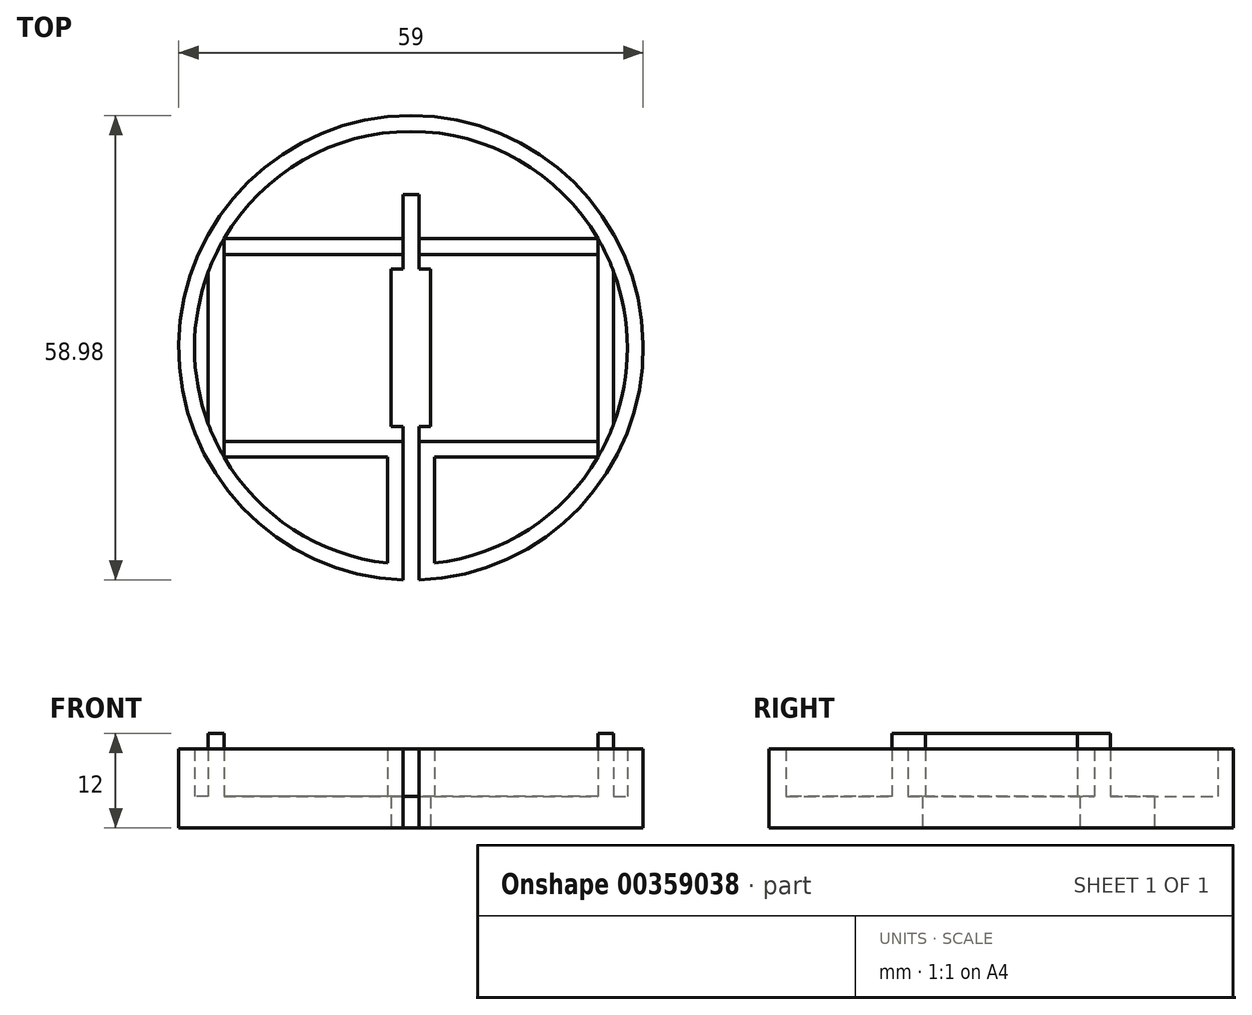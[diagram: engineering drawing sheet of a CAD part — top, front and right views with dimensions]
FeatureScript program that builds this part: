
annotation { "Feature Type Name" : "Feature", "Feature Type Description" : "" }
export const myFeature = defineFeature(function(context is Context, id is Id, definition is map)
    precondition{}
    {
        {
            var Q0;
            Q0=qCreatedBy(makeId("Top.planeOp"),FACE);
            var sketch = newSketch(context, id + "F0", { "sketchPlane" : qUnion([Q0])});
            skCircle(sketch, "E0", {"center": v(0, 0) * mm, "radius": 29.5 * mm});
            skPoint(sketch, "E1.middle", {"position": v(0, 29.5) * mm});
            skLineSegment(sketch, "E2.top", {"start": v(-1, -29.48) * mm, "end": v(1, -29.48) * mm});
            skLineSegment(sketch, "E2.left", {"start": v(-1, 29.48) * mm, "end": v(-1, -29.48) * mm});
            skLineSegment(sketch, "E2.right", {"start": v(1, 29.48) * mm, "end": v(1, -29.48) * mm});
            skLineSegment(sketch, "E3.bottom", {"start": v(-2.5, 10) * mm, "end": v(2.5, 10) * mm});
            skLineSegment(sketch, "E3.top", {"start": v(-2.5, -10) * mm, "end": v(2.5, -10) * mm});
            skLineSegment(sketch, "E3.left", {"start": v(-2.5, 10) * mm, "end": v(-2.5, -10) * mm});
            skLineSegment(sketch, "E3.right", {"start": v(2.5, 10) * mm, "end": v(2.5, -10) * mm});
            skLineSegment(sketch, "E4.top", {"start": v(-1, 19.48) * mm, "end": v(1, 19.48) * mm});
            skLineSegment(sketch, "E4.left", {"start": v(-1, 29.48) * mm, "end": v(-1, 19.48) * mm});
            skLineSegment(sketch, "E4.right", {"start": v(1, 29.48) * mm, "end": v(1, 19.48) * mm});
            skLineSegment(sketch, "E5", {"start": v(-23.75, 17.5) * mm, "end": v(-23.75, -17.5) * mm});
            skLineSegment(sketch, "E6", {"start": v(23.75, 17.5) * mm, "end": v(23.75, -17.5) * mm});
            skLineSegment(sketch, "E7", {"start": v(25.75, 14.4) * mm, "end": v(25.75, -14.4) * mm});
            skCircle(sketch, "E8", {"center": v(0, 0) * mm, "radius": 27.5 * mm});
            skLineSegment(sketch, "E9", {"start": v(-25.75, 14.4) * mm, "end": v(-25.75, -14.4) * mm});
            skLineSegment(sketch, "E10", {"start": v(-23.75, 13.87) * mm, "end": v(23.75, 13.87) * mm});
            skLineSegment(sketch, "E11", {"start": v(-23.75, 11.87) * mm, "end": v(23.75, 11.87) * mm});
            skLineSegment(sketch, "E12", {"start": v(-23.75, -13.87) * mm, "end": v(23.75, -13.87) * mm});
            skLineSegment(sketch, "E13", {"start": v(-23.75, -11.87) * mm, "end": v(23.75, -11.87) * mm});
            skLineSegment(sketch, "E14", {"start": v(-3, -27.34) * mm, "end": v(-3, -13.87) * mm});
            skLineSegment(sketch, "E15", {"start": v(3, -13.87) * mm, "end": v(3, -27.34) * mm});
            skSolve(sketch);
        }
        {
            var Q0;
            {var subQ0=sQuery(id+"F0.wireOp",EDGE,"E3.left");Q0=makeQuery(id+"F0.imprint","IMPRINT",FACE,{"disambiguationData":[TD([[makeQuery(id+"F0.imprint","IMPRINT",EDGE,{"derivedFrom":subQ0}),-1.0]])]});}
            var Q1;
            {var subQ1=sQuery(id+"F0.wireOp",EDGE,"E5");var subQ8=makeQuery(id+"F0.imprint","INTERSECT",VERTEX,{"derivedFrom":[subQ1,sQuery(id+"F0.wireOp",EDGE,"E11")]});Q1=makeQuery(id+"F0.imprint","IMPRINT",FACE,{"disambiguationData":[TD([[makeQuery(id+"F0.imprint","IMPRINT",EDGE,{"disambiguationData":[TD([[subQ8,-1.0]])],"derivedFrom":subQ1}),-1.0]])]});}
            var Q2;
            {var subQ0=sQuery(id+"F0.wireOp",EDGE,"E9");var subQ1=sQuery(id+"F0.wireOp",EDGE,"E8");var subQ2=makeQuery(id+"F0.imprint","INTERSECT",VERTEX,{"disambiguationData":[OD(0.0)],"derivedFrom":[subQ1,subQ0]});Q2=makeQuery(id+"F0.imprint","IMPRINT",FACE,{"disambiguationData":[TD([[makeQuery(id+"F0.imprint","IMPRINT",EDGE,{"disambiguationData":[TD([[subQ2,-1.0]])],"derivedFrom":subQ1}),1.0]])]});}
            var Q3;
            {var subQ0=sQuery(id+"F0.wireOp",EDGE,"E9");var subQ1=sQuery(id+"F0.wireOp",EDGE,"E0");var subQ2=makeQuery(id+"F0.imprint","INTERSECT",VERTEX,{"disambiguationData":[OD(0.0)],"derivedFrom":[subQ1,subQ0]});Q3=makeQuery(id+"F0.imprint","IMPRINT",FACE,{"disambiguationData":[TD([[makeQuery(id+"F0.imprint","IMPRINT",EDGE,{"disambiguationData":[TD([[subQ2,-1.0]])],"derivedFrom":subQ1}),1.0]])]});}
            var Q4;
            {var subQ0=sQuery(id+"F0.wireOp",EDGE,"E5");var subQ1=sQuery(id+"F0.wireOp",EDGE,"E0");var subQ2=makeQuery(id+"F0.imprint","INTERSECT",VERTEX,{"disambiguationData":[OD(0.0)],"derivedFrom":[subQ1,subQ0]});Q4=makeQuery(id+"F0.imprint","IMPRINT",FACE,{"disambiguationData":[TD([[makeQuery(id+"F0.imprint","IMPRINT",EDGE,{"disambiguationData":[TD([[subQ2,-1.0]])],"derivedFrom":subQ1}),1.0]])]});}
            var Q5;
            {var subQ0=sQuery(id+"F0.wireOp",EDGE,"E4.left");var subQ1=sQuery(id+"F0.wireOp",EDGE,"E0");var subQ2=makeQuery(id+"F0.imprint","INTERSECT",VERTEX,{"derivedFrom":[subQ1,subQ0]});Q5=makeQuery(id+"F0.imprint","IMPRINT",FACE,{"disambiguationData":[TD([[makeQuery(id+"F0.imprint","IMPRINT",EDGE,{"disambiguationData":[TD([[subQ2,-1.0]])],"derivedFrom":subQ1}),1.0]])]});}
            var Q6;
            {var subQ1=sQuery(id+"F0.wireOp",EDGE,"E2.left");var subQ3=sQuery(id+"F0.wireOp",EDGE,"E10");var subQ4=makeQuery(id+"F0.imprint","INTERSECT",VERTEX,{"derivedFrom":[subQ1,subQ3]});Q6=makeQuery(id+"F0.imprint","IMPRINT",FACE,{"disambiguationData":[TD([[makeQuery(id+"F0.imprint","IMPRINT",EDGE,{"disambiguationData":[TD([[subQ4,1.0]])],"derivedFrom":subQ1}),-1.0]])]});}
            var Q7;
            {var subQ0=sQuery(id+"F0.wireOp",EDGE,"E10");var subQ1=sQuery(id+"F0.wireOp",EDGE,"E2.left");var subQ2=makeQuery(id+"F0.imprint","INTERSECT",VERTEX,{"derivedFrom":[subQ1,subQ0]});Q7=makeQuery(id+"F0.imprint","IMPRINT",FACE,{"disambiguationData":[TD([[makeQuery(id+"F0.imprint","IMPRINT",EDGE,{"disambiguationData":[TD([[subQ2,-1.0]])],"derivedFrom":subQ1}),-1.0]])]});}
            var Q8;
            {var subQ0=sQuery(id+"F0.wireOp",EDGE,"E4.right");var subQ1=sQuery(id+"F0.wireOp",EDGE,"E0");var subQ2=makeQuery(id+"F0.imprint","INTERSECT",VERTEX,{"derivedFrom":[subQ1,subQ0]});Q8=makeQuery(id+"F0.imprint","IMPRINT",FACE,{"disambiguationData":[TD([[makeQuery(id+"F0.imprint","IMPRINT",EDGE,{"disambiguationData":[TD([[subQ2,1.0]])],"derivedFrom":subQ1}),1.0]])]});}
            var Q9;
            {var subQ0=sQuery(id+"F0.wireOp",EDGE,"E4.left");var subQ1=sQuery(id+"F0.wireOp",EDGE,"E0");var subQ2=makeQuery(id+"F0.imprint","INTERSECT",VERTEX,{"derivedFrom":[subQ1,subQ0]});Q9=makeQuery(id+"F0.imprint","IMPRINT",FACE,{"disambiguationData":[TD([[makeQuery(id+"F0.imprint","IMPRINT",EDGE,{"disambiguationData":[TD([[subQ2,1.0]])],"derivedFrom":subQ1}),1.0]])]});}
            var Q10;
            {var subQ0=sQuery(id+"F0.wireOp",EDGE,"E4.top");Q10=makeQuery(id+"F0.imprint","IMPRINT",FACE,{"disambiguationData":[TD([[makeQuery(id+"F0.imprint","IMPRINT",EDGE,{"derivedFrom":subQ0}),1.0]])]});}
            var Q11;
            {var subQ1=sQuery(id+"F0.wireOp",EDGE,"E2.right");var subQ3=sQuery(id+"F0.wireOp",EDGE,"E10");var subQ4=makeQuery(id+"F0.imprint","INTERSECT",VERTEX,{"derivedFrom":[subQ1,subQ3]});Q11=makeQuery(id+"F0.imprint","IMPRINT",FACE,{"disambiguationData":[TD([[makeQuery(id+"F0.imprint","IMPRINT",EDGE,{"disambiguationData":[TD([[subQ4,1.0]])],"derivedFrom":subQ1}),1.0]])]});}
            var Q12;
            {var subQ0=sQuery(id+"F0.wireOp",EDGE,"E10");var subQ1=sQuery(id+"F0.wireOp",EDGE,"E2.right");var subQ2=makeQuery(id+"F0.imprint","INTERSECT",VERTEX,{"derivedFrom":[subQ1,subQ0]});Q12=makeQuery(id+"F0.imprint","IMPRINT",FACE,{"disambiguationData":[TD([[makeQuery(id+"F0.imprint","IMPRINT",EDGE,{"disambiguationData":[TD([[subQ2,-1.0]])],"derivedFrom":subQ1}),1.0]])]});}
            var Q13;
            {var subQ0=sQuery(id+"F0.wireOp",EDGE,"E3.right");Q13=makeQuery(id+"F0.imprint","IMPRINT",FACE,{"disambiguationData":[TD([[makeQuery(id+"F0.imprint","IMPRINT",EDGE,{"derivedFrom":subQ0}),1.0]])]});}
            var Q14;
            {var subQ4=sQuery(id+"F0.wireOp",EDGE,"E13");var subQ6=sQuery(id+"F0.wireOp",EDGE,"E2.right");var subQ8=makeQuery(id+"F0.imprint","INTERSECT",VERTEX,{"derivedFrom":[subQ6,subQ4]});Q14=makeQuery(id+"F0.imprint","IMPRINT",FACE,{"disambiguationData":[TD([[makeQuery(id+"F0.imprint","IMPRINT",EDGE,{"disambiguationData":[TD([[subQ8,-1.0]])],"derivedFrom":subQ6}),1.0]])]});}
            var Q15;
            {var subQ3=sQuery(id+"F0.wireOp",EDGE,"E15");Q15=makeQuery(id+"F0.imprint","IMPRINT",FACE,{"disambiguationData":[TD([[makeQuery(id+"F0.imprint","IMPRINT",EDGE,{"derivedFrom":subQ3}),1.0]])]});}
            var Q16;
            {var subQ2=sQuery(id+"F0.wireOp",EDGE,"E2.left");var subQ6=sQuery(id+"F0.wireOp",EDGE,"E13");var subQ8=makeQuery(id+"F0.imprint","INTERSECT",VERTEX,{"derivedFrom":[subQ2,subQ6]});Q16=makeQuery(id+"F0.imprint","IMPRINT",FACE,{"disambiguationData":[TD([[makeQuery(id+"F0.imprint","IMPRINT",EDGE,{"disambiguationData":[TD([[subQ8,-1.0]])],"derivedFrom":subQ2}),-1.0]])]});}
            var Q17;
            {var subQ3=sQuery(id+"F0.wireOp",EDGE,"E14");Q17=makeQuery(id+"F0.imprint","IMPRINT",FACE,{"disambiguationData":[TD([[makeQuery(id+"F0.imprint","IMPRINT",EDGE,{"derivedFrom":subQ3}),1.0]])]});}
            var Q18;
            {var subQ3=sQuery(id+"F0.wireOp",EDGE,"E8");var subQ8=makeQuery(id+"F0.imprint","INTERSECT",VERTEX,{"derivedFrom":[subQ3,sQuery(id+"F0.wireOp",EDGE,"E14")]});Q18=makeQuery(id+"F0.imprint","IMPRINT",FACE,{"disambiguationData":[TD([[makeQuery(id+"F0.imprint","IMPRINT",EDGE,{"disambiguationData":[TD([[subQ8,-1.0]])],"derivedFrom":subQ3}),-1.0]])]});}
            var Q19;
            {var subQ0=sQuery(id+"F0.wireOp",EDGE,"E5");var subQ1=sQuery(id+"F0.wireOp",EDGE,"E0");var subQ2=makeQuery(id+"F0.imprint","INTERSECT",VERTEX,{"disambiguationData":[OD(1.0)],"derivedFrom":[subQ1,subQ0]});Q19=makeQuery(id+"F0.imprint","IMPRINT",FACE,{"disambiguationData":[TD([[makeQuery(id+"F0.imprint","IMPRINT",EDGE,{"disambiguationData":[TD([[subQ2,1.0]])],"derivedFrom":subQ1}),1.0]])]});}
            var Q20;
            {var subQ0=sQuery(id+"F0.wireOp",EDGE,"E8");var subQ1=makeQuery(id+"F0.imprint","INTERSECT",VERTEX,{"derivedFrom":[subQ0,sQuery(id+"F0.wireOp",EDGE,"E15")]});Q20=makeQuery(id+"F0.imprint","IMPRINT",FACE,{"disambiguationData":[TD([[makeQuery(id+"F0.imprint","IMPRINT",EDGE,{"disambiguationData":[TD([[subQ1,1.0]])],"derivedFrom":subQ0}),-1.0]])]});}
            var Q21;
            {var subQ1=sQuery(id+"F0.wireOp",EDGE,"E6");var subQ4=makeQuery(id+"F0.imprint","INTERSECT",VERTEX,{"derivedFrom":[subQ1,sQuery(id+"F0.wireOp",EDGE,"E11")]});Q21=makeQuery(id+"F0.imprint","IMPRINT",FACE,{"disambiguationData":[TD([[makeQuery(id+"F0.imprint","IMPRINT",EDGE,{"disambiguationData":[TD([[subQ4,-1.0]])],"derivedFrom":subQ1}),1.0]])]});}
            var Q22;
            {var subQ0=sQuery(id+"F0.wireOp",EDGE,"E8");var subQ1=sQuery(id+"F0.wireOp",EDGE,"E7");var subQ2=makeQuery(id+"F0.imprint","INTERSECT",VERTEX,{"disambiguationData":[OD(0.0)],"derivedFrom":[subQ1,subQ0]});Q22=makeQuery(id+"F0.imprint","IMPRINT",FACE,{"disambiguationData":[TD([[makeQuery(id+"F0.imprint","IMPRINT",EDGE,{"disambiguationData":[TD([[subQ2,-1.0]])],"derivedFrom":subQ1}),1.0]])]});}
            var Q23;
            {var subQ0=sQuery(id+"F0.wireOp",EDGE,"E7");var subQ1=sQuery(id+"F0.wireOp",EDGE,"E0");var subQ2=makeQuery(id+"F0.imprint","INTERSECT",VERTEX,{"disambiguationData":[OD(0.0)],"derivedFrom":[subQ1,subQ0]});Q23=makeQuery(id+"F0.imprint","IMPRINT",FACE,{"disambiguationData":[TD([[makeQuery(id+"F0.imprint","IMPRINT",EDGE,{"disambiguationData":[TD([[subQ2,1.0]])],"derivedFrom":subQ1}),1.0]])]});}
            var Q24;
            {var subQ0=sQuery(id+"F0.wireOp",EDGE,"E6");var subQ1=sQuery(id+"F0.wireOp",EDGE,"E0");var subQ2=makeQuery(id+"F0.imprint","INTERSECT",VERTEX,{"disambiguationData":[OD(0.0)],"derivedFrom":[subQ1,subQ0]});Q24=makeQuery(id+"F0.imprint","IMPRINT",FACE,{"disambiguationData":[TD([[makeQuery(id+"F0.imprint","IMPRINT",EDGE,{"disambiguationData":[TD([[subQ2,1.0]])],"derivedFrom":subQ1}),1.0]])]});}
            var Q25;
            {var subQ0=sQuery(id+"F0.wireOp",EDGE,"E6");var subQ1=sQuery(id+"F0.wireOp",EDGE,"E0");var subQ2=makeQuery(id+"F0.imprint","INTERSECT",VERTEX,{"disambiguationData":[OD(1.0)],"derivedFrom":[subQ1,subQ0]});Q25=makeQuery(id+"F0.imprint","IMPRINT",FACE,{"disambiguationData":[TD([[makeQuery(id+"F0.imprint","IMPRINT",EDGE,{"disambiguationData":[TD([[subQ2,-1.0]])],"derivedFrom":subQ1}),1.0]])]});}
            var Q26;
            {var subQ5=sQuery(id+"F0.wireOp",EDGE,"E14");Q26=makeQuery(id+"F0.imprint","IMPRINT",FACE,{"disambiguationData":[TD([[makeQuery(id+"F0.imprint","IMPRINT",EDGE,{"derivedFrom":subQ5}),-1.0]])]});}
            var Q27;
            {var subQ5=sQuery(id+"F0.wireOp",EDGE,"E15");Q27=makeQuery(id+"F0.imprint","IMPRINT",FACE,{"disambiguationData":[TD([[makeQuery(id+"F0.imprint","IMPRINT",EDGE,{"derivedFrom":subQ5}),-1.0]])]});}
            extrude(context, id + "F1", {"entities" : qUnion([Q0, Q1, Q2, Q3, Q4, Q5, Q6, Q7, Q8, Q9, Q10, Q11, Q12, Q13, Q14, Q15, Q16, Q17, Q18, Q19, Q20, Q21, Q22, Q23, Q24, Q25, Q26, Q27]), "depth" : 4 * mm});
        }
        {
            var Q0;
            {var subQ1=sQuery(id+"F0.wireOp",EDGE,"E5");var subQ8=makeQuery(id+"F0.imprint","INTERSECT",VERTEX,{"derivedFrom":[subQ1,sQuery(id+"F0.wireOp",EDGE,"E11")]});Q0=makeQuery(id+"F0.imprint","IMPRINT",FACE,{"disambiguationData":[TD([[makeQuery(id+"F0.imprint","IMPRINT",EDGE,{"disambiguationData":[TD([[subQ8,-1.0]])],"derivedFrom":subQ1}),-1.0]])]});}
            var Q1;
            {var subQ1=sQuery(id+"F0.wireOp",EDGE,"E6");var subQ4=makeQuery(id+"F0.imprint","INTERSECT",VERTEX,{"derivedFrom":[subQ1,sQuery(id+"F0.wireOp",EDGE,"E11")]});Q1=makeQuery(id+"F0.imprint","IMPRINT",FACE,{"disambiguationData":[TD([[makeQuery(id+"F0.imprint","IMPRINT",EDGE,{"disambiguationData":[TD([[subQ4,-1.0]])],"derivedFrom":subQ1}),1.0]])]});}
            extrude(context, id + "F2", {"entities" : qUnion([Q0, Q1]), "operationType" : NewBodyOperationType.ADD, "depth" : 12 * mm});
        }
        {
            var Q0;
            {var subQ1=sQuery(id+"F0.wireOp",EDGE,"E5");var subQ8=makeQuery(id+"F0.imprint","INTERSECT",VERTEX,{"derivedFrom":[subQ1,sQuery(id+"F0.wireOp",EDGE,"E11")]});Q0=makeQuery(id+"F0.imprint","IMPRINT",FACE,{"disambiguationData":[TD([[makeQuery(id+"F0.imprint","IMPRINT",EDGE,{"disambiguationData":[TD([[subQ8,-1.0]])],"derivedFrom":subQ1}),-1.0]])]});}
            var Q1;
            {var subQ0=sQuery(id+"F0.wireOp",EDGE,"E5");var subQ1=sQuery(id+"F0.wireOp",EDGE,"E0");var subQ2=makeQuery(id+"F0.imprint","INTERSECT",VERTEX,{"disambiguationData":[OD(1.0)],"derivedFrom":[subQ1,subQ0]});Q1=makeQuery(id+"F0.imprint","IMPRINT",FACE,{"disambiguationData":[TD([[makeQuery(id+"F0.imprint","IMPRINT",EDGE,{"disambiguationData":[TD([[subQ2,1.0]])],"derivedFrom":subQ1}),1.0]])]});}
            var Q2;
            {var subQ3=sQuery(id+"F0.wireOp",EDGE,"E8");var subQ8=makeQuery(id+"F0.imprint","INTERSECT",VERTEX,{"derivedFrom":[subQ3,sQuery(id+"F0.wireOp",EDGE,"E14")]});Q2=makeQuery(id+"F0.imprint","IMPRINT",FACE,{"disambiguationData":[TD([[makeQuery(id+"F0.imprint","IMPRINT",EDGE,{"disambiguationData":[TD([[subQ8,-1.0]])],"derivedFrom":subQ3}),-1.0]])]});}
            var Q3;
            {var subQ5=sQuery(id+"F0.wireOp",EDGE,"E14");Q3=makeQuery(id+"F0.imprint","IMPRINT",FACE,{"disambiguationData":[TD([[makeQuery(id+"F0.imprint","IMPRINT",EDGE,{"derivedFrom":subQ5}),-1.0]])]});}
            var Q4;
            {var subQ2=sQuery(id+"F0.wireOp",EDGE,"E2.left");var subQ6=sQuery(id+"F0.wireOp",EDGE,"E13");var subQ8=makeQuery(id+"F0.imprint","INTERSECT",VERTEX,{"derivedFrom":[subQ2,subQ6]});Q4=makeQuery(id+"F0.imprint","IMPRINT",FACE,{"disambiguationData":[TD([[makeQuery(id+"F0.imprint","IMPRINT",EDGE,{"disambiguationData":[TD([[subQ8,-1.0]])],"derivedFrom":subQ2}),-1.0]])]});}
            var Q5;
            {var subQ4=sQuery(id+"F0.wireOp",EDGE,"E13");var subQ6=sQuery(id+"F0.wireOp",EDGE,"E2.right");var subQ8=makeQuery(id+"F0.imprint","INTERSECT",VERTEX,{"derivedFrom":[subQ6,subQ4]});Q5=makeQuery(id+"F0.imprint","IMPRINT",FACE,{"disambiguationData":[TD([[makeQuery(id+"F0.imprint","IMPRINT",EDGE,{"disambiguationData":[TD([[subQ8,-1.0]])],"derivedFrom":subQ6}),1.0]])]});}
            var Q6;
            {var subQ5=sQuery(id+"F0.wireOp",EDGE,"E15");Q6=makeQuery(id+"F0.imprint","IMPRINT",FACE,{"disambiguationData":[TD([[makeQuery(id+"F0.imprint","IMPRINT",EDGE,{"derivedFrom":subQ5}),-1.0]])]});}
            var Q7;
            {var subQ0=sQuery(id+"F0.wireOp",EDGE,"E8");var subQ1=makeQuery(id+"F0.imprint","INTERSECT",VERTEX,{"derivedFrom":[subQ0,sQuery(id+"F0.wireOp",EDGE,"E15")]});Q7=makeQuery(id+"F0.imprint","IMPRINT",FACE,{"disambiguationData":[TD([[makeQuery(id+"F0.imprint","IMPRINT",EDGE,{"disambiguationData":[TD([[subQ1,1.0]])],"derivedFrom":subQ0}),-1.0]])]});}
            var Q8;
            {var subQ1=sQuery(id+"F0.wireOp",EDGE,"E6");var subQ4=makeQuery(id+"F0.imprint","INTERSECT",VERTEX,{"derivedFrom":[subQ1,sQuery(id+"F0.wireOp",EDGE,"E11")]});Q8=makeQuery(id+"F0.imprint","IMPRINT",FACE,{"disambiguationData":[TD([[makeQuery(id+"F0.imprint","IMPRINT",EDGE,{"disambiguationData":[TD([[subQ4,-1.0]])],"derivedFrom":subQ1}),1.0]])]});}
            var Q9;
            {var subQ0=sQuery(id+"F0.wireOp",EDGE,"E6");var subQ1=sQuery(id+"F0.wireOp",EDGE,"E0");var subQ2=makeQuery(id+"F0.imprint","INTERSECT",VERTEX,{"disambiguationData":[OD(0.0)],"derivedFrom":[subQ1,subQ0]});Q9=makeQuery(id+"F0.imprint","IMPRINT",FACE,{"disambiguationData":[TD([[makeQuery(id+"F0.imprint","IMPRINT",EDGE,{"disambiguationData":[TD([[subQ2,1.0]])],"derivedFrom":subQ1}),1.0]])]});}
            var Q10;
            {var subQ0=sQuery(id+"F0.wireOp",EDGE,"E6");var subQ1=sQuery(id+"F0.wireOp",EDGE,"E0");var subQ2=makeQuery(id+"F0.imprint","INTERSECT",VERTEX,{"disambiguationData":[OD(1.0)],"derivedFrom":[subQ1,subQ0]});Q10=makeQuery(id+"F0.imprint","IMPRINT",FACE,{"disambiguationData":[TD([[makeQuery(id+"F0.imprint","IMPRINT",EDGE,{"disambiguationData":[TD([[subQ2,-1.0]])],"derivedFrom":subQ1}),1.0]])]});}
            var Q11;
            {var subQ0=sQuery(id+"F0.wireOp",EDGE,"E4.right");var subQ1=sQuery(id+"F0.wireOp",EDGE,"E0");var subQ2=makeQuery(id+"F0.imprint","INTERSECT",VERTEX,{"derivedFrom":[subQ1,subQ0]});Q11=makeQuery(id+"F0.imprint","IMPRINT",FACE,{"disambiguationData":[TD([[makeQuery(id+"F0.imprint","IMPRINT",EDGE,{"disambiguationData":[TD([[subQ2,1.0]])],"derivedFrom":subQ1}),1.0]])]});}
            var Q12;
            {var subQ0=sQuery(id+"F0.wireOp",EDGE,"E4.left");var subQ1=sQuery(id+"F0.wireOp",EDGE,"E0");var subQ2=makeQuery(id+"F0.imprint","INTERSECT",VERTEX,{"derivedFrom":[subQ1,subQ0]});Q12=makeQuery(id+"F0.imprint","IMPRINT",FACE,{"disambiguationData":[TD([[makeQuery(id+"F0.imprint","IMPRINT",EDGE,{"disambiguationData":[TD([[subQ2,-1.0]])],"derivedFrom":subQ1}),1.0]])]});}
            var Q13;
            {var subQ0=sQuery(id+"F0.wireOp",EDGE,"E5");var subQ1=sQuery(id+"F0.wireOp",EDGE,"E0");var subQ2=makeQuery(id+"F0.imprint","INTERSECT",VERTEX,{"disambiguationData":[OD(0.0)],"derivedFrom":[subQ1,subQ0]});Q13=makeQuery(id+"F0.imprint","IMPRINT",FACE,{"disambiguationData":[TD([[makeQuery(id+"F0.imprint","IMPRINT",EDGE,{"disambiguationData":[TD([[subQ2,-1.0]])],"derivedFrom":subQ1}),1.0]])]});}
            var Q14;
            {var subQ0=sQuery(id+"F0.wireOp",EDGE,"E10");var subQ1=sQuery(id+"F0.wireOp",EDGE,"E2.left");var subQ2=makeQuery(id+"F0.imprint","INTERSECT",VERTEX,{"derivedFrom":[subQ1,subQ0]});Q14=makeQuery(id+"F0.imprint","IMPRINT",FACE,{"disambiguationData":[TD([[makeQuery(id+"F0.imprint","IMPRINT",EDGE,{"disambiguationData":[TD([[subQ2,-1.0]])],"derivedFrom":subQ1}),-1.0]])]});}
            var Q15;
            {var subQ0=sQuery(id+"F0.wireOp",EDGE,"E10");var subQ1=sQuery(id+"F0.wireOp",EDGE,"E2.right");var subQ2=makeQuery(id+"F0.imprint","INTERSECT",VERTEX,{"derivedFrom":[subQ1,subQ0]});Q15=makeQuery(id+"F0.imprint","IMPRINT",FACE,{"disambiguationData":[TD([[makeQuery(id+"F0.imprint","IMPRINT",EDGE,{"disambiguationData":[TD([[subQ2,-1.0]])],"derivedFrom":subQ1}),1.0]])]});}
            extrude(context, id + "F3", {"entities" : qUnion([Q0, Q1, Q2, Q3, Q4, Q5, Q6, Q7, Q8, Q9, Q10, Q11, Q12, Q13, Q14, Q15]), "operationType" : NewBodyOperationType.ADD, "depth" : 10 * mm});
        }
        {
            var Q0;
            {var subQ0=sQuery(id+"F0.wireOp",EDGE,"E4.left");var subQ1=sQuery(id+"F0.wireOp",EDGE,"E0");var subQ2=makeQuery(id+"F0.imprint","INTERSECT",VERTEX,{"derivedFrom":[subQ1,subQ0]});Q0=makeQuery(id+"F0.imprint","IMPRINT",FACE,{"disambiguationData":[TD([[makeQuery(id+"F0.imprint","IMPRINT",EDGE,{"disambiguationData":[TD([[subQ2,1.0]])],"derivedFrom":subQ1}),1.0]])]});}
            extrude(context, id + "F4", {"entities" : qUnion([Q0]), "operationType" : NewBodyOperationType.ADD, "depth" : 10 * mm});
        }
    });
